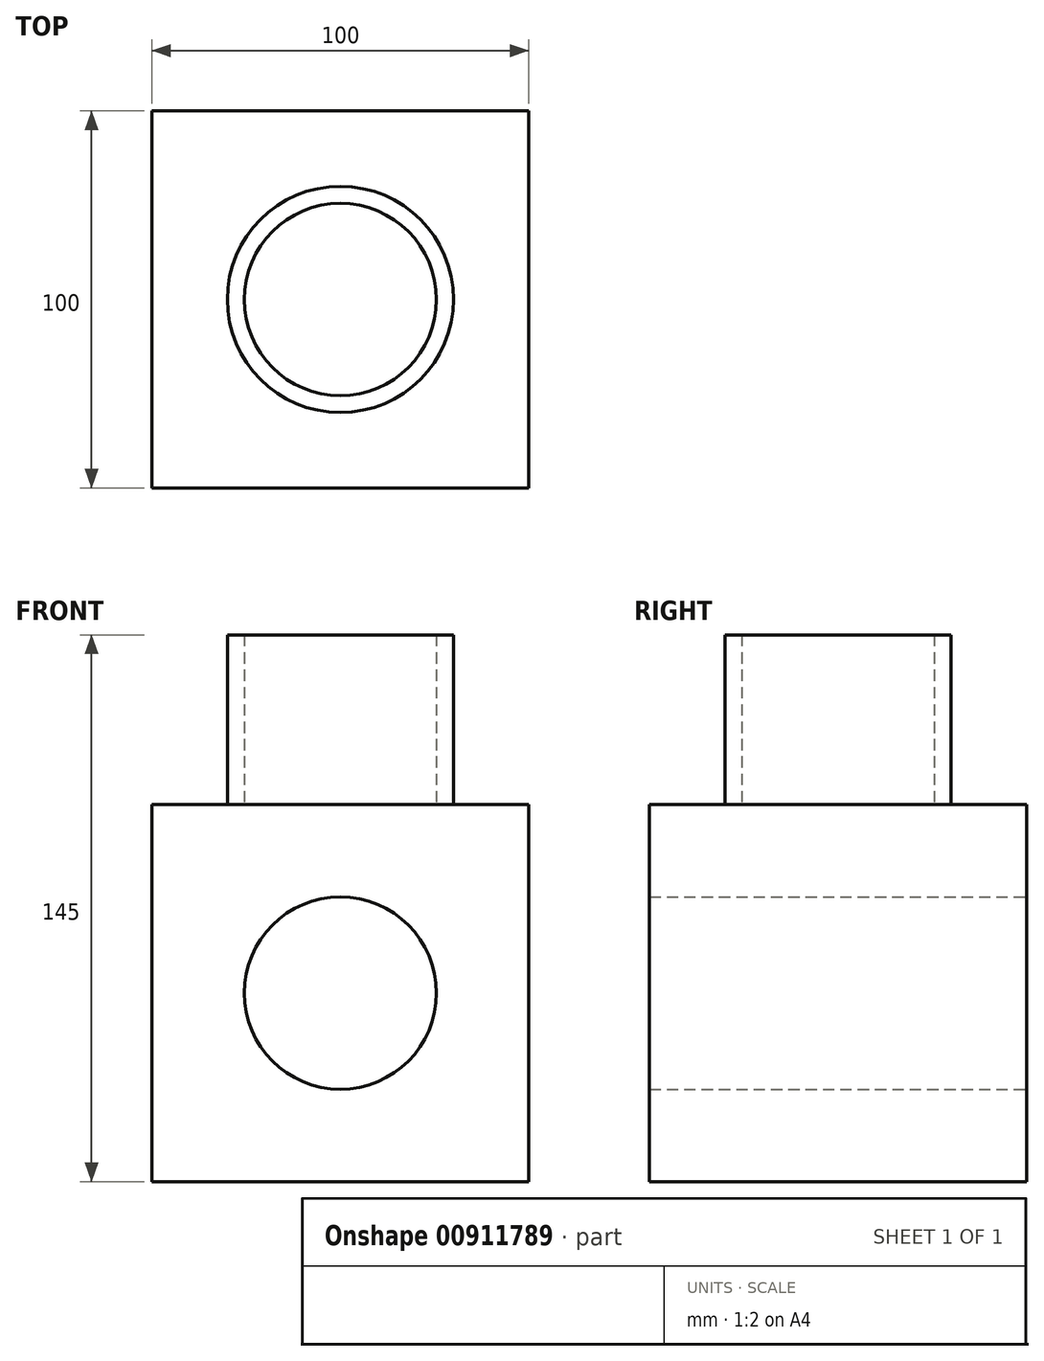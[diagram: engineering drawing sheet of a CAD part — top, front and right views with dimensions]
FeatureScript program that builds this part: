
annotation { "Feature Type Name" : "Feature", "Feature Type Description" : "" }
export const myFeature = defineFeature(function(context is Context, id is Id, definition is map)
    precondition{}
    {
        {
            var Q0;
            Q0=qCreatedBy(makeId("Front.planeOp"),FACE);
            var sketch = newSketch(context, id + "F0", { "sketchPlane" : qUnion([Q0])});
            skCircle(sketch, "E0", {"center": v(0, 0) * mm, "radius": 25.5 * mm});
            skLineSegment(sketch, "E1.bottom", {"start": v(-50, 50) * mm, "end": v(50, 50) * mm});
            skLineSegment(sketch, "E1.top", {"start": v(-50, -50) * mm, "end": v(50, -50) * mm});
            skLineSegment(sketch, "E1.left", {"start": v(-50, 50) * mm, "end": v(-50, -50) * mm});
            skLineSegment(sketch, "E1.right", {"start": v(50, 50) * mm, "end": v(50, -50) * mm});
            skSolve(sketch);
        }
        {
            var Q0;
            Q0=makeQuery(id+"F0.imprint","IMPRINT",FACE,{"disambiguationData":[TD([[makeQuery(id+"F0.imprint","IMPRINT",EDGE,{"derivedFrom":sQuery(id+"F0.wireOp",EDGE,"E0")}),-1.0]])]});
            extrude(context, id + "F1", {"entities" : qUnion([Q0]), "depth" : 100 * mm, "offsetDistance" : 25 * mm, "symmetric" : true});
        }
        {
            var Q0;
            Q0=makeQuery(id+"F1.opExtrude","SWEPT_FACE",FACE,{"disambiguationData":[OSD([sQuery(id+"F0.wireOp",EDGE,"E1.bottom")])]});
            var sketch = newSketch(context, id + "F2", { "sketchPlane" : qUnion([Q0])});
            skCircle(sketch, "E2", {"center": v(0, 0) * mm, "radius": 30 * mm});
            skCircle(sketch, "E3", {"center": v(0, 0) * mm, "radius": 25.5 * mm});
            skSolve(sketch);
        }
        {
            var Q0;
            Q0=makeQuery(id+"F2.imprint","IMPRINT",FACE,{"disambiguationData":[TD([[makeQuery(id+"F2.imprint","IMPRINT",EDGE,{"derivedFrom":sQuery(id+"F2.wireOp",EDGE,"E2")}),1.0]])]});
            var Q1;
            Q1=sQuery(id+"F2.wireOp",EDGE,"E3");
            var Q2;
            Q2=sQuery(id+"F2.wireOp",EDGE,"E2");
            extrude(context, id + "F3", {"entities" : qUnion([Q0]), "operationType" : NewBodyOperationType.ADD, "surfaceEntities" : qUnion([Q1, Q2]), "depth" : 45 * mm, "offsetDistance" : 25 * mm});
        }
    });
